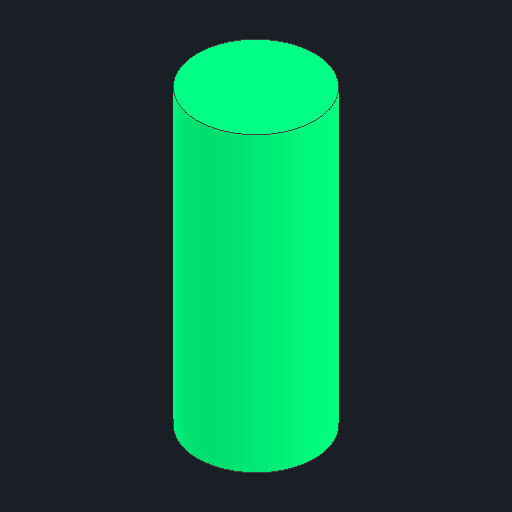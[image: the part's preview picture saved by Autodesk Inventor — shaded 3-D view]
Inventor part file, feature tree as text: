
AUTODESK INVENTOR PART (.ipt)
format: ipt  version: 2025.2 (Build 292293000, 293)  size: 83,968 bytes
history: native  units: in
note: dims shown in document units (in); Inventor stores cm internally (conversion verified against a paired STEP export)
features: other x3, sketch x1
ambient origin geometry x8: Origin, YZ Plane, XZ Plane, XY Plane, X Axis, Y Axis, Z Axis, Center Point
bodies: Solid1 (feature_tree)
feature tree (4):
  other  "26650(Green).ipt"
  other  "Solid1::26650(Green).ipt"
  other  "TaggingFeature1"
  sketch  "Sketch1"  dims[d0=0.3937in]
